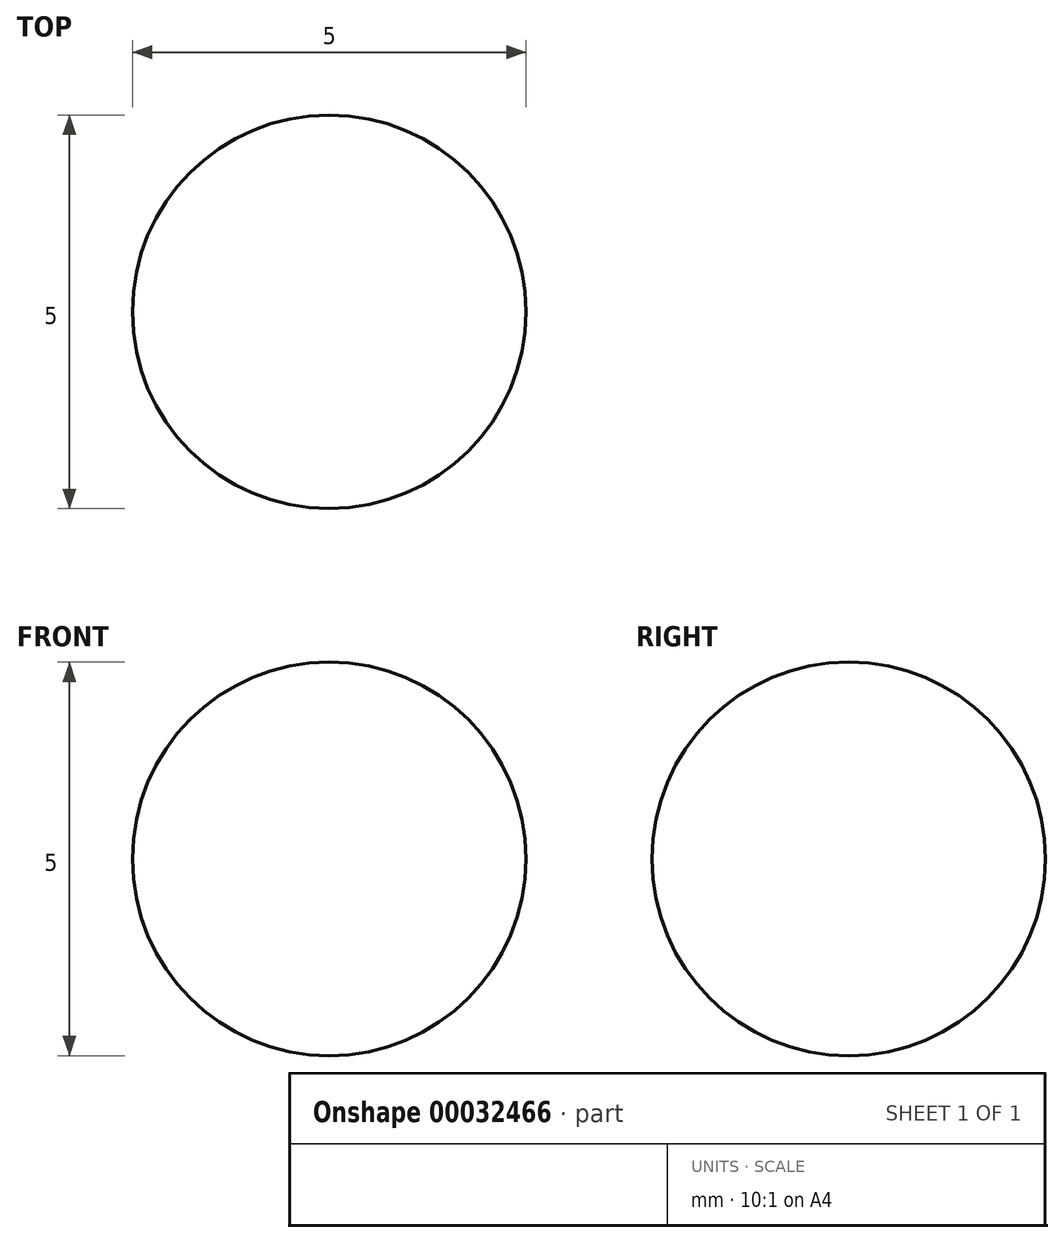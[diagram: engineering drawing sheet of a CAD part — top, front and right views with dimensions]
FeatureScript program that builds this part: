
annotation { "Feature Type Name" : "Feature", "Feature Type Description" : "" }
export const myFeature = defineFeature(function(context is Context, id is Id, definition is map)
    precondition{}
    {
        {
            var Q0;
            Q0=qCreatedBy(makeId("Top.planeOp"),FACE);
            var sketch = newSketch(context, id + "F0", { "sketchPlane" : qUnion([Q0])});
            skCircle(sketch, "E0", {"center": v(0, 0) * mm, "radius": 2.5 * mm});
            skLineSegment(sketch, "E1", {"start": v(0, 0) * mm, "end": v(0, -3.98) * mm});
            skLineSegment(sketch, "E2", {"start": v(0, 0) * mm, "end": v(0, 5.03) * mm});
            skSolve(sketch);
        }
        {
            var Q0;
            {var subQ1=sQuery(id+"F0.wireOp",EDGE,"E0");var subQ3=sQuery(id+"F0.wireOp",EDGE,"E1");var subQ5=makeQuery(id+"F0.imprint","INTERSECT",VERTEX,{"derivedFrom":[subQ1,subQ3]});Q0=makeQuery(id+"F0.imprint","IMPRINT",FACE,{"disambiguationData":[TD([[makeQuery(id+"F0.imprint","IMPRINT",EDGE,{"disambiguationData":[TD([[subQ5,1.0]])],"derivedFrom":subQ1}),1.0]])]});}
            var Q1;
            Q1=sQuery(id+"F0.wireOp",EDGE,"E1");
            revolve(context, id + "F1", {"entities" : qUnion([Q0]), "axis" : qUnion([Q1]), "revolveType" : RevolveType.FULL});
        }
    });
